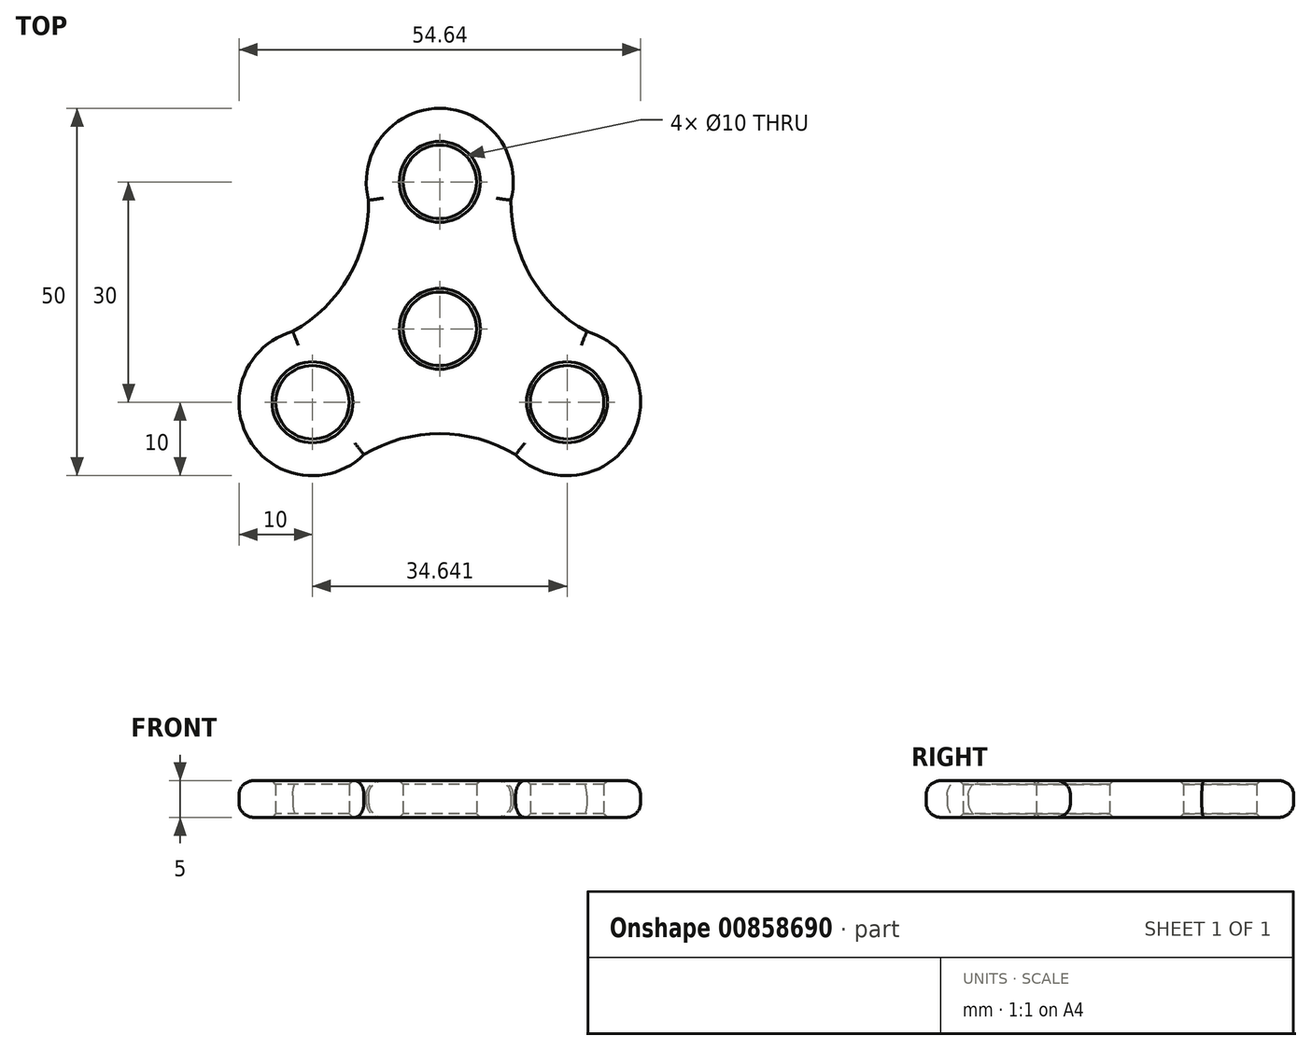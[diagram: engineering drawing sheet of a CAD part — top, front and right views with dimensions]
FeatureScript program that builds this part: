
annotation { "Feature Type Name" : "Feature", "Feature Type Description" : "" }
export const myFeature = defineFeature(function(context is Context, id is Id, definition is map)
    precondition{}
    {
        {
            var Q0;
            Q0=qCreatedBy(makeId("Top.planeOp"),FACE);
            var sketch = newSketch(context, id + "F0", { "sketchPlane" : qUnion([Q0])});
            skArc(sketch, "E0", {"start": v(9.68, 17.5) * mm, "mid": v(0, 30) * mm, "end": v(-9.68, 17.5) * mm});
            skCircle(sketch, "E1", {"center": v(0, 20) * mm, "radius": 5 * mm});
            skArc(sketch, "E2.1.0", {"start": v(-20, -0.36) * mm, "mid": v(-25.98, -15) * mm, "end": v(-10.31, -17.14) * mm});
            skArc(sketch, "E2.2.0", {"start": v(10.31, -17.14) * mm, "mid": v(25.98, -15) * mm, "end": v(20, -0.36) * mm});
            skPoint(sketch, "E2.center", {"position": v(0, 0) * mm});
            skCircle(sketch, "E3", {"center": v(17.32, -10) * mm, "radius": 5 * mm});
            skCircle(sketch, "E4", {"center": v(-17.32, -10) * mm, "radius": 5 * mm});
            skCircle(sketch, "E5", {"center": v(0, 0) * mm, "radius": 5 * mm});
            skArc(sketch, "E6", {"start": v(-20, -0.36) * mm, "mid": v(-12.36, 7.14) * mm, "end": v(-9.68, 17.5) * mm});
            skArc(sketch, "E7", {"start": v(9.68, 17.5) * mm, "mid": v(12.36, 7.14) * mm, "end": v(20, -0.36) * mm});
            skArc(sketch, "E8", {"start": v(10.31, -17.14) * mm, "mid": v(0, -14.27) * mm, "end": v(-10.31, -17.14) * mm});
            skSolve(sketch);
        }
        {
            var Q0;
            Q0=qSketchRegion(id+"F0",true);
            extrude(context, id + "F1", {"entities" : qUnion([Q0]), "depth" : 5 * mm, "offsetDistance" : 25 * mm});
        }
        {
            var Q0;
            Q0=makeQuery(id+"F1.opExtrude","CAP_EDGE",EDGE,{"disambiguationData":[OSD([sQuery(id+"F0.wireOp",EDGE,"E8")])],"isStart":false});
            var Q1;
            Q1=makeQuery(id+"F1.opExtrude","CAP_EDGE",EDGE,{"disambiguationData":[OSD([sQuery(id+"F0.wireOp",EDGE,"E2.2.0")])],"isStart":false});
            var Q2;
            Q2=makeQuery(id+"F1.opExtrude","CAP_EDGE",EDGE,{"disambiguationData":[OSD([sQuery(id+"F0.wireOp",EDGE,"E7")])],"isStart":false});
            var Q3;
            Q3=makeQuery(id+"F1.opExtrude","CAP_EDGE",EDGE,{"disambiguationData":[OSD([sQuery(id+"F0.wireOp",EDGE,"E0")])],"isStart":false});
            var Q4;
            Q4=makeQuery(id+"F1.opExtrude","CAP_EDGE",EDGE,{"disambiguationData":[OSD([sQuery(id+"F0.wireOp",EDGE,"E6")])],"isStart":false});
            var Q5;
            Q5=makeQuery(id+"F1.opExtrude","CAP_EDGE",EDGE,{"disambiguationData":[OSD([sQuery(id+"F0.wireOp",EDGE,"E2.1.0")])],"isStart":false});
            var Q6;
            Q6=makeQuery(id+"F1.opExtrude","CAP_EDGE",EDGE,{"disambiguationData":[OSD([sQuery(id+"F0.wireOp",EDGE,"E7")])],"isStart":true});
            var Q7;
            Q7=makeQuery(id+"F1.opExtrude","CAP_EDGE",EDGE,{"disambiguationData":[OSD([sQuery(id+"F0.wireOp",EDGE,"E2.2.0")])],"isStart":true});
            var Q8;
            Q8=makeQuery(id+"F1.opExtrude","CAP_EDGE",EDGE,{"disambiguationData":[OSD([sQuery(id+"F0.wireOp",EDGE,"E8")])],"isStart":true});
            var Q9;
            Q9=makeQuery(id+"F1.opExtrude","CAP_EDGE",EDGE,{"disambiguationData":[OSD([sQuery(id+"F0.wireOp",EDGE,"E2.1.0")])],"isStart":true});
            var Q10;
            Q10=makeQuery(id+"F1.opExtrude","CAP_EDGE",EDGE,{"disambiguationData":[OSD([sQuery(id+"F0.wireOp",EDGE,"E6")])],"isStart":true});
            var Q11;
            Q11=makeQuery(id+"F1.opExtrude","CAP_EDGE",EDGE,{"disambiguationData":[OSD([sQuery(id+"F0.wireOp",EDGE,"E0")])],"isStart":true});
            fillet(context, id + "F2", {"entities" : qUnion([Q0, Q1, Q2, Q3, Q4, Q5, Q6, Q7, Q8, Q9, Q10, Q11]), "radius" : 2 * mm, "tangentPropagation" : true, "allowEdgeOverflow" : false});
        }
        {
            var Q0;
            Q0=makeQuery(id+"F1.opExtrude","CAP_EDGE",EDGE,{"disambiguationData":[OSD([sQuery(id+"F0.wireOp",EDGE,"E3")])],"isStart":false});
            var Q1;
            Q1=makeQuery(id+"F1.opExtrude","CAP_EDGE",EDGE,{"disambiguationData":[OSD([sQuery(id+"F0.wireOp",EDGE,"E5")])],"isStart":false});
            var Q2;
            Q2=makeQuery(id+"F1.opExtrude","CAP_EDGE",EDGE,{"disambiguationData":[OSD([sQuery(id+"F0.wireOp",EDGE,"E4")])],"isStart":false});
            var Q3;
            Q3=makeQuery(id+"F1.opExtrude","CAP_EDGE",EDGE,{"disambiguationData":[OSD([sQuery(id+"F0.wireOp",EDGE,"E1")])],"isStart":false});
            var Q4;
            Q4=makeQuery(id+"F1.opExtrude","CAP_EDGE",EDGE,{"disambiguationData":[OSD([sQuery(id+"F0.wireOp",EDGE,"E1")])],"isStart":true});
            var Q5;
            Q5=makeQuery(id+"F1.opExtrude","CAP_EDGE",EDGE,{"disambiguationData":[OSD([sQuery(id+"F0.wireOp",EDGE,"E5")])],"isStart":true});
            var Q6;
            Q6=makeQuery(id+"F1.opExtrude","CAP_EDGE",EDGE,{"disambiguationData":[OSD([sQuery(id+"F0.wireOp",EDGE,"E4")])],"isStart":true});
            var Q7;
            Q7=makeQuery(id+"F1.opExtrude","CAP_EDGE",EDGE,{"disambiguationData":[OSD([sQuery(id+"F0.wireOp",EDGE,"E3")])],"isStart":true});
            chamfer(context, id + "F3", {"entities" : qUnion([Q0, Q1, Q2, Q3, Q4, Q5, Q6, Q7]), "width" : .5 * mm, "tangentPropagation" : true});
        }
    });
